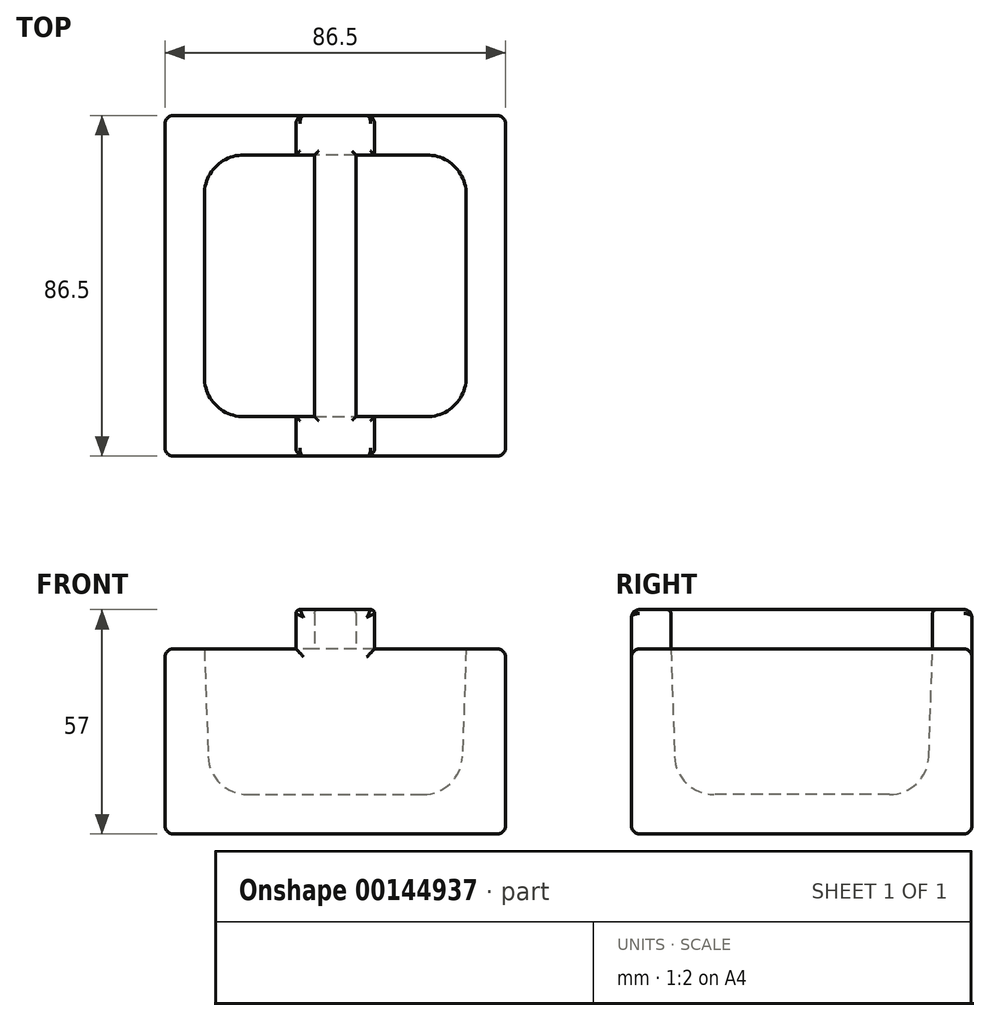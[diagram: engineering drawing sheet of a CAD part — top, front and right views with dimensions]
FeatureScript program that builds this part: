
annotation { "Feature Type Name" : "Feature", "Feature Type Description" : "" }
export const myFeature = defineFeature(function(context is Context, id is Id, definition is map)
    precondition{}
    {
        {
            var Q0;
            Q0=qCreatedBy(makeId("Top.planeOp"),FACE);
            var sketch = newSketch(context, id + "F0", { "sketchPlane" : qUnion([Q0])});
            skLineSegment(sketch, "E0.bottom", {"start": v(0, 0) * mm, "end": v(86.5, 0) * mm});
            skLineSegment(sketch, "E0.top", {"start": v(0, 86.5) * mm, "end": v(86.5, 86.5) * mm});
            skLineSegment(sketch, "E0.left", {"start": v(0, 0) * mm, "end": v(0, 86.5) * mm});
            skLineSegment(sketch, "E0.right", {"start": v(86.5, 0) * mm, "end": v(86.5, 86.5) * mm});
            skSolve(sketch);
        }
        {
            var Q0;
            Q0=makeQuery(id+"F0.imprint","IMPRINT",FACE,{"disambiguationData":[TD([[makeQuery(id+"F0.imprint","IMPRINT",EDGE,{"derivedFrom":sQuery(id+"F0.wireOp",EDGE,"E0.bottom")}),1.0]])]});
            extrude(context, id + "F1", {"entities" : qUnion([Q0]), "depth" : 47 * mm});
        }
        {
            var Q0;
            Q0=makeQuery(id+"F1.opExtrude","CAP_FACE",FACE,{"disambiguationData":[OSD([sQuery(id+"F0.wireOp",EDGE,"E0.bottom"),sQuery(id+"F0.wireOp",EDGE,"E0.top"),sQuery(id+"F0.wireOp",EDGE,"E0.left"),sQuery(id+"F0.wireOp",EDGE,"E0.right")])],"isStart":false});
            var sketch = newSketch(context, id + "F2", { "sketchPlane" : qUnion([Q0])});
            skLineSegment(sketch, "E1.0", {"start": v(0, 0) * mm, "end": v(0, 86.5) * mm});
            skLineSegment(sketch, "E1.1", {"start": v(0, 0) * mm, "end": v(86.5, 0) * mm});
            skLineSegment(sketch, "E2.bottom", {"start": v(10, 76.5) * mm, "end": v(76.5, 76.5) * mm});
            skLineSegment(sketch, "E2.top", {"start": v(10, 10) * mm, "end": v(76.5, 10) * mm});
            skLineSegment(sketch, "E2.left", {"start": v(10, 76.5) * mm, "end": v(10, 10) * mm});
            skLineSegment(sketch, "E2.right", {"start": v(76.5, 76.5) * mm, "end": v(76.5, 10) * mm});
            skSolve(sketch);
        }
        {
            var Q0;
            Q0=makeQuery(id+"F2.imprint","IMPRINT",FACE,{"disambiguationData":[TD([[makeQuery(id+"F2.imprint","IMPRINT",EDGE,{"derivedFrom":sQuery(id+"F2.wireOp",EDGE,"E2.bottom")}),-1.0]])]});
            extrude(context, id + "F3", {"entities" : qUnion([Q0]), "operationType" : NewBodyOperationType.REMOVE, "oppositeDirection" : true, "depth" : 37 * mm, "hasDraft" : true, "draftAngle" : 2 * degree, "draftPullDirection" : true});
        }
        {
            var Q0;
            Q0=makeQuery(id+"F3.boolean.opBoolean","COPY",EDGE,{"derivedFrom":makeQuery(id+"F3.opExtrude","SWEPT_EDGE",EDGE,{"disambiguationData":[OSD([sQuery(id+"F2.wireOp",EDGE,"E2.top"),sQuery(id+"F2.wireOp",EDGE,"E2.left")])]})});
            var Q1;
            Q1=makeQuery(id+"F3.boolean.opBoolean","COPY",EDGE,{"derivedFrom":makeQuery(id+"F3.opExtrude","SWEPT_EDGE",EDGE,{"disambiguationData":[OSD([sQuery(id+"F2.wireOp",EDGE,"E2.top"),sQuery(id+"F2.wireOp",EDGE,"E2.right")])]})});
            var Q2;
            Q2=makeQuery(id+"F3.boolean.opBoolean","COPY",EDGE,{"derivedFrom":makeQuery(id+"F3.opExtrude","SWEPT_EDGE",EDGE,{"disambiguationData":[OSD([sQuery(id+"F2.wireOp",EDGE,"E2.bottom"),sQuery(id+"F2.wireOp",EDGE,"E2.right")])]})});
            var Q3;
            Q3=makeQuery(id+"F3.boolean.opBoolean","COPY",EDGE,{"derivedFrom":makeQuery(id+"F3.opExtrude","SWEPT_EDGE",EDGE,{"disambiguationData":[OSD([sQuery(id+"F2.wireOp",EDGE,"E2.bottom"),sQuery(id+"F2.wireOp",EDGE,"E2.left")])]})});
            var Q4;
            Q4=makeQuery(id+"F3.boolean.opBoolean","COPY",FACE,{"derivedFrom":makeQuery(id+"F3.opExtrude","CAP_FACE",FACE,{"disambiguationData":[OSD([sQuery(id+"F2.wireOp",EDGE,"E2.bottom"),sQuery(id+"F2.wireOp",EDGE,"E2.top"),sQuery(id+"F2.wireOp",EDGE,"E2.left"),sQuery(id+"F2.wireOp",EDGE,"E2.right")])],"isStart":false})});
            fillet(context, id + "F4", {"entities" : qUnion([Q0, Q1, Q2, Q3, Q4]), "radius" : 10 * mm, "tangentPropagation" : true, "allowEdgeOverflow" : false});
        }
        {
            var Q0;
            Q0=makeQuery(id+"F1.opExtrude","CAP_FACE",FACE,{"disambiguationData":[OSD([sQuery(id+"F0.wireOp",EDGE,"E0.bottom"),sQuery(id+"F0.wireOp",EDGE,"E0.top"),sQuery(id+"F0.wireOp",EDGE,"E0.left"),sQuery(id+"F0.wireOp",EDGE,"E0.right")])],"isStart":false});
            var sketch = newSketch(context, id + "F5", { "sketchPlane" : qUnion([Q0])});
            skLineSegment(sketch, "E3.0", {"start": v(0, 0) * mm, "end": v(86.5, 0) * mm});
            skLineSegment(sketch, "E3.1", {"start": v(0, 0) * mm, "end": v(0, 86.5) * mm});
            skLineSegment(sketch, "E4.bottom", {"start": v(38, 0) * mm, "end": v(48.5, 0) * mm});
            skLineSegment(sketch, "E4.top", {"start": v(38, 86.5) * mm, "end": v(48.5, 86.5) * mm});
            skLineSegment(sketch, "E4.left", {"start": v(38, 0) * mm, "end": v(38, 86.5) * mm});
            skLineSegment(sketch, "E4.right", {"start": v(48.5, 0) * mm, "end": v(48.5, 86.5) * mm});
            skLineSegment(sketch, "E5", {"start": v(43.25, 0) * mm, "end": v(43.25, 86.5) * mm, "construction": true});
            skLineSegment(sketch, "E6.bottom", {"start": v(33.25, 0) * mm, "end": v(53.25, 0) * mm});
            skLineSegment(sketch, "E6.top", {"start": v(33.25, 86.5) * mm, "end": v(53.25, 86.5) * mm});
            skLineSegment(sketch, "E6.left", {"start": v(33.25, 0) * mm, "end": v(33.25, 86.5) * mm});
            skLineSegment(sketch, "E6.right", {"start": v(53.25, 0) * mm, "end": v(53.25, 86.5) * mm});
            skLineSegment(sketch, "E7.0", {"start": v(20, 76.5) * mm, "end": v(66.5, 76.5) * mm});
            skLineSegment(sketch, "E7.1", {"start": v(20, 10) * mm, "end": v(66.5, 10) * mm});
            skLineSegment(sketch, "E8", {"start": v(35.76, 4.8) * mm, "end": v(49.22, 4.8) * mm});
            skLineSegment(sketch, "E9", {"start": v(35.67, 81.7) * mm, "end": v(49.6, 81.7) * mm});
            skSolve(sketch);
        }
        {
            var Q0;
            {var subQ0=sQuery(id+"F5.wireOp",EDGE,"E6.bottom");var subQ1=sQuery(id+"F5.wireOp",EDGE,"E4.left");var subQ2=makeQuery(id+"F5.imprint","INTERSECT",VERTEX,{"derivedFrom":[subQ1,subQ0]});Q0=makeQuery(id+"F5.imprint","IMPRINT",FACE,{"disambiguationData":[TD([[makeQuery(id+"F5.imprint","IMPRINT",EDGE,{"disambiguationData":[TD([[subQ2,-1.0]])],"derivedFrom":subQ1}),1.0]])]});}
            var Q1;
            {var subQ0=sQuery(id+"F5.wireOp",EDGE,"E6.top");var subQ1=sQuery(id+"F5.wireOp",EDGE,"E4.right");var subQ2=makeQuery(id+"F5.imprint","INTERSECT",VERTEX,{"derivedFrom":[subQ1,subQ0]});Q1=makeQuery(id+"F5.imprint","IMPRINT",FACE,{"disambiguationData":[TD([[makeQuery(id+"F5.imprint","IMPRINT",EDGE,{"disambiguationData":[TD([[subQ2,1.0]])],"derivedFrom":subQ1}),-1.0]])]});}
            var Q2;
            {var subQ0=sQuery(id+"F5.wireOp",EDGE,"E6.top");var subQ1=sQuery(id+"F5.wireOp",EDGE,"E4.left");var subQ2=makeQuery(id+"F5.imprint","INTERSECT",VERTEX,{"derivedFrom":[subQ1,subQ0]});Q2=makeQuery(id+"F5.imprint","IMPRINT",FACE,{"disambiguationData":[TD([[makeQuery(id+"F5.imprint","IMPRINT",EDGE,{"disambiguationData":[TD([[subQ2,1.0]])],"derivedFrom":subQ1}),1.0]])]});}
            var Q3;
            {var subQ0=sQuery(id+"F5.wireOp",EDGE,"E6.bottom");var subQ1=sQuery(id+"F5.wireOp",EDGE,"E4.right");var subQ2=makeQuery(id+"F5.imprint","INTERSECT",VERTEX,{"derivedFrom":[subQ1,subQ0]});Q3=makeQuery(id+"F5.imprint","IMPRINT",FACE,{"disambiguationData":[TD([[makeQuery(id+"F5.imprint","IMPRINT",EDGE,{"disambiguationData":[TD([[subQ2,-1.0]])],"derivedFrom":subQ1}),-1.0]])]});}
            var Q4;
            {var subQ0=sQuery(id+"F5.wireOp",EDGE,"E6.bottom");var subQ1=sQuery(id+"F5.wireOp",EDGE,"E4.left");var subQ2=makeQuery(id+"F5.imprint","INTERSECT",VERTEX,{"derivedFrom":[subQ1,subQ0]});Q4=makeQuery(id+"F5.imprint","IMPRINT",FACE,{"disambiguationData":[TD([[makeQuery(id+"F5.imprint","IMPRINT",EDGE,{"disambiguationData":[TD([[subQ2,-1.0]])],"derivedFrom":subQ1}),-1.0]])]});}
            var Q5;
            {var subQ0=sQuery(id+"F5.wireOp",EDGE,"E6.top");var subQ1=sQuery(id+"F5.wireOp",EDGE,"E4.left");var subQ2=makeQuery(id+"F5.imprint","INTERSECT",VERTEX,{"derivedFrom":[subQ1,subQ0]});Q5=makeQuery(id+"F5.imprint","IMPRINT",FACE,{"disambiguationData":[TD([[makeQuery(id+"F5.imprint","IMPRINT",EDGE,{"disambiguationData":[TD([[subQ2,1.0]])],"derivedFrom":subQ1}),-1.0]])]});}
            extrude(context, id + "F6", {"entities" : qUnion([Q0, Q1, Q2, Q3, Q4, Q5]), "operationType" : NewBodyOperationType.ADD, "depth" : 10 * mm});
        }
        {
            var Q0;
            {var subQ0=sQuery(id+"F5.wireOp",EDGE,"E6.bottom");Q0=makeQuery(id+"F6.boolean.opBoolean","MERGE",FACE,{"derivedFrom":[makeQuery(id+"F1.opExtrude","SWEPT_FACE",FACE,{"disambiguationData":[OSD([sQuery(id+"F0.wireOp",EDGE,"E0.bottom")])]}),makeQuery(id+"F6.opExtrude","SWEPT_FACE",FACE,{"disambiguationData":[OSD([subQ0]),TDD([makeQuery(id+"F5.imprint","IMPRINT",EDGE,{"disambiguationData":[TD([[makeQuery(id+"F5.imprint","INTERSECT",VERTEX,{"derivedFrom":[sQuery(id+"F5.wireOp",EDGE,"E4.left"),subQ0]}),1.0]])],"derivedFrom":subQ0})])]}),makeQuery(id+"F6.opExtrude","SWEPT_FACE",FACE,{"disambiguationData":[OSD([subQ0]),TDD([makeQuery(id+"F5.imprint","IMPRINT",EDGE,{"disambiguationData":[TD([[makeQuery(id+"F5.imprint","INTERSECT",VERTEX,{"derivedFrom":[sQuery(id+"F5.wireOp",EDGE,"E4.right"),subQ0]}),-1.0]])],"derivedFrom":subQ0})])]})]});}
            var Q1;
            Q1=makeQuery(id+"F1.opExtrude","SWEPT_FACE",FACE,{"disambiguationData":[OSD([sQuery(id+"F0.wireOp",EDGE,"E0.right")])]});
            var Q2;
            {var subQ0=sQuery(id+"F5.wireOp",EDGE,"E6.top");var subQ1=sQuery(id+"F0.wireOp",EDGE,"E0.top");Q2=makeQuery(id+"F6.boolean.opBoolean","MERGE",FACE,{"derivedFrom":[makeQuery(id+"F1.opExtrude","SWEPT_FACE",FACE,{"disambiguationData":[OSD([subQ1])]}),makeQuery(id+"F6.opExtrude","SWEPT_FACE",FACE,{"disambiguationData":[OSD([subQ0]),TDD([makeQuery(id+"F5.imprint","IMPRINT",EDGE,{"disambiguationData":[TD([[makeQuery(id+"F5.imprint","INTERSECT",VERTEX,{"derivedFrom":[sQuery(id+"F5.wireOp",EDGE,"E4.left"),subQ0]}),1.0]])],"derivedFrom":subQ0})])]}),makeQuery(id+"F6.opExtrude","SWEPT_FACE",FACE,{"disambiguationData":[OSD([subQ0]),TDD([makeQuery(id+"F5.imprint","IMPRINT",EDGE,{"disambiguationData":[TD([[makeQuery(id+"F5.imprint","INTERSECT",VERTEX,{"derivedFrom":[sQuery(id+"F5.wireOp",EDGE,"E4.right"),subQ0]}),-1.0]])],"derivedFrom":subQ0})])]})]});}
            var Q3;
            Q3=makeQuery(id+"F1.opExtrude","SWEPT_FACE",FACE,{"disambiguationData":[OSD([sQuery(id+"F0.wireOp",EDGE,"E0.left")])]});
            fillet(context, id + "F7", {"entities" : qUnion([Q0, Q1, Q2, Q3]), "radius" : 2 * mm, "tangentPropagation" : true, "allowEdgeOverflow" : false});
        }
        {
            var Q0;
            Q0=makeQuery(id+"F6.opExtrude","CAP_FACE",FACE,{"disambiguationData":[OSD([sQuery(id+"F5.wireOp",EDGE,"E4.right"),sQuery(id+"F5.wireOp",EDGE,"E6.bottom"),sQuery(id+"F5.wireOp",EDGE,"E6.right"),sQuery(id+"F5.wireOp",EDGE,"E7.1")])],"isStart":false});
            var Q1;
            Q1=makeQuery(id+"F6.opExtrude","CAP_FACE",FACE,{"disambiguationData":[OSD([sQuery(id+"F5.wireOp",EDGE,"E4.left"),sQuery(id+"F5.wireOp",EDGE,"E6.bottom"),sQuery(id+"F5.wireOp",EDGE,"E6.left"),sQuery(id+"F5.wireOp",EDGE,"E7.1")])],"isStart":false});
            var Q2;
            Q2=makeQuery(id+"F6.opExtrude","CAP_FACE",FACE,{"disambiguationData":[OSD([sQuery(id+"F5.wireOp",EDGE,"E4.right"),sQuery(id+"F5.wireOp",EDGE,"E6.top"),sQuery(id+"F5.wireOp",EDGE,"E6.right"),sQuery(id+"F5.wireOp",EDGE,"E7.0")])],"isStart":false});
            var Q3;
            Q3=makeQuery(id+"F6.opExtrude","CAP_FACE",FACE,{"disambiguationData":[OSD([sQuery(id+"F5.wireOp",EDGE,"E4.left"),sQuery(id+"F5.wireOp",EDGE,"E6.top"),sQuery(id+"F5.wireOp",EDGE,"E6.left"),sQuery(id+"F5.wireOp",EDGE,"E7.0")])],"isStart":false});
            fillet(context, id + "F8", {"entities" : qUnion([Q0, Q1, Q2, Q3]), "radius" : 1 * mm, "tangentPropagation" : true, "allowEdgeOverflow" : false});
        }
    });
